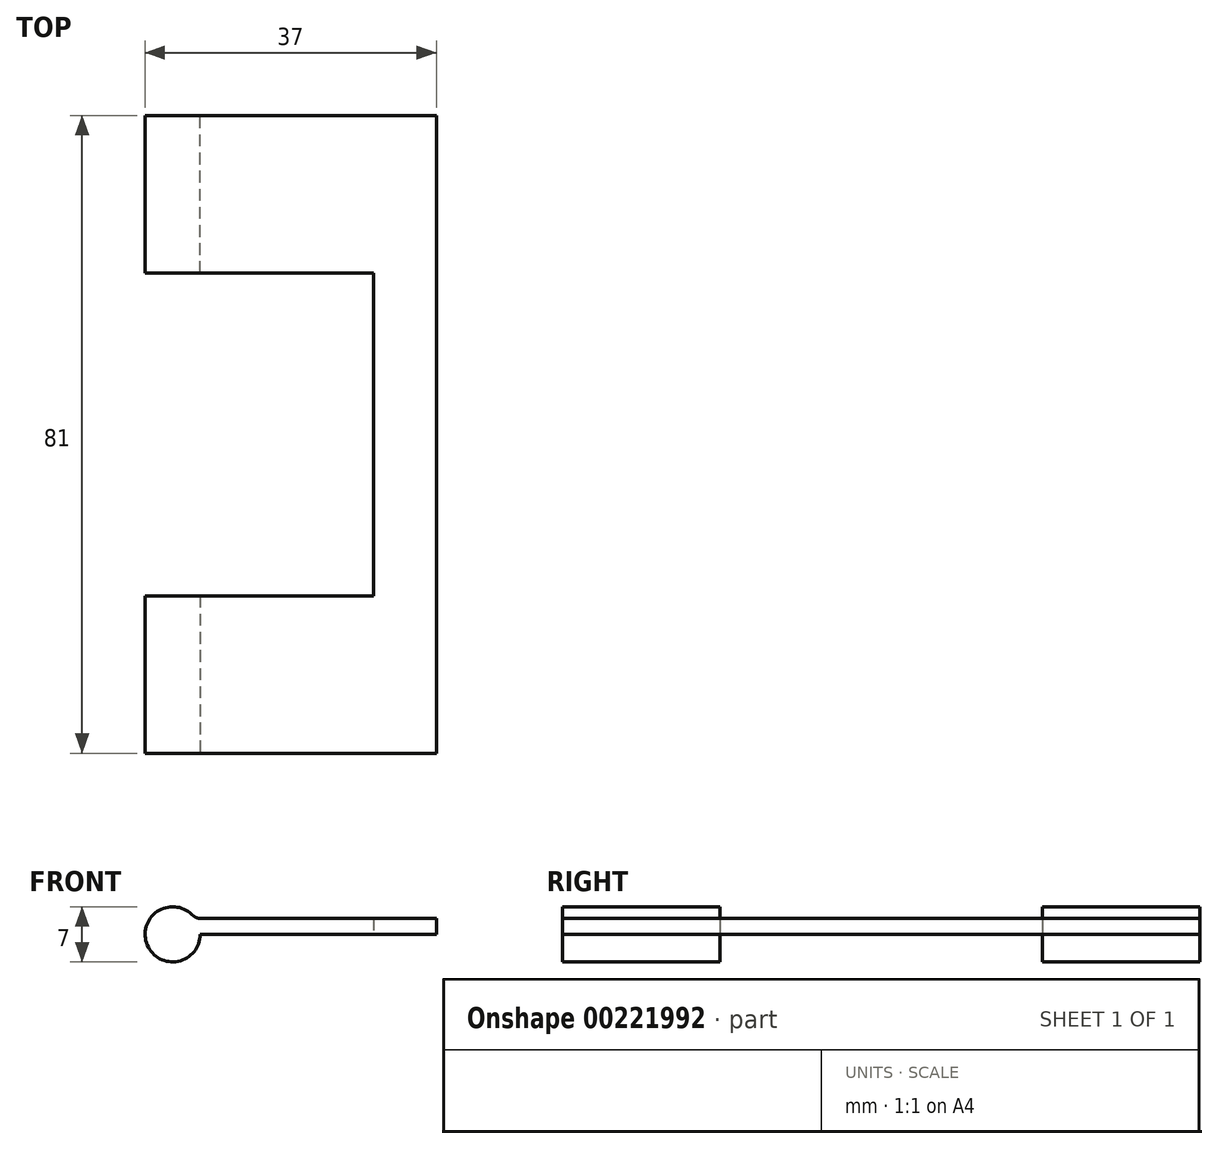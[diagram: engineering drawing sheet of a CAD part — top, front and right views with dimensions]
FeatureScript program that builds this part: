
annotation { "Feature Type Name" : "Feature", "Feature Type Description" : "" }
export const myFeature = defineFeature(function(context is Context, id is Id, definition is map)
    precondition{}
    {
        {
            var Q0;
            Q0=qCreatedBy(makeId("Top.planeOp"),FACE);
            var sketch = newSketch(context, id + "F0", { "sketchPlane" : qUnion([Q0])});
            skLineSegment(sketch, "E0", {"start": v(0, 40.5) * mm, "end": v(30, 40.5) * mm});
            skLineSegment(sketch, "E1", {"start": v(30, 40.5) * mm, "end": v(30, 0) * mm});
            skLineSegment(sketch, "E2", {"start": v(30, 0) * mm, "end": v(22, 0) * mm});
            skLineSegment(sketch, "E3", {"start": v(22, 0) * mm, "end": v(22, 20.5) * mm});
            skLineSegment(sketch, "E4", {"start": v(22, 20.5) * mm, "end": v(0, 20.5) * mm});
            skLineSegment(sketch, "E5", {"start": v(0, 20.5) * mm, "end": v(0, 40.5) * mm});
            skSolve(sketch);
        }
        {
            var Q0;
            Q0 = qSketchRegion(id + "F0", true);
            extrude(context, id + "F1", {"entities" : qUnion([Q0]), "depth" : 2 * mm});
        }
        {
            var Q0;
            Q0=makeQuery(id+"F1.opExtrude","SWEPT_FACE",FACE,{"disambiguationData":[OSD([sQuery(id+"F0.wireOp",EDGE,"E0")])]});
            cPlane(context, id + "F2", {"entities" : qUnion([Q0]), "cplaneType" : CPlaneType.OFFSET, "offset" : 0 * mm, "width" : 150 * mm, "height" : 150 * mm});
        }
        {
            var Q0;
            Q0=qCreatedBy(id+"F2.planeOp",FACE);
            var sketch = newSketch(context, id + "F3", { "sketchPlane" : qUnion([Q0])});
            skCircle(sketch, "E6", {"center": v(3.5, 0) * mm, "radius": 3.5 * mm});
            skLineSegment(sketch, "E7", {"start": v(0, 0) * mm, "end": v(0, 2) * mm});
            skFitSpline(sketch, "E8", {"points": [v(1.07, 2.52) * mm, v(0, 2) * mm], "startDerivative": vector(-0.77, -0.74) * mm, "endDerivative": vector(-1.07, 0) * mm});
            skSolve(sketch);
        }
        {
            var Q0;
            Q0 = qSketchRegion(id + "F3", true);
            var Q1;
            Q1=makeQuery(id+"F1.opExtrude","SWEPT_FACE",FACE,{"disambiguationData":[OSD([sQuery(id+"F0.wireOp",EDGE,"E4")])]});
            extrude(context, id + "F4", {"entities" : qUnion([Q0]), "operationType" : NewBodyOperationType.ADD, "endBound" : BoundingType.UP_TO_SURFACE, "oppositeDirection" : true, "endBoundEntityFace" : qUnion([Q1]), "depth" : 25 * mm});
        }
        {
            var Q0;
            Q0=makeQuery(id+"F1.opExtrude","SWEPT_BODY",BODY,{"disambiguationData":[OSD([sQuery(id+"F0.wireOp",EDGE,"E0"),sQuery(id+"F0.wireOp",EDGE,"E1"),sQuery(id+"F0.wireOp",EDGE,"E3"),sQuery(id+"F0.wireOp",EDGE,"E4"),sQuery(id+"F0.wireOp",EDGE,"E5"),sQuery(id+"F0.wireOp",EDGE,"E2")])]});
            var Q1;
            Q1=qCreatedBy(makeId("Front.planeOp"),FACE);
            mirror(context, id + "F5", {"operationType" : NewBodyOperationType.ADD, "entities" : qUnion([Q0]), "mirrorPlane" : qUnion([Q1])});
        }
    });
